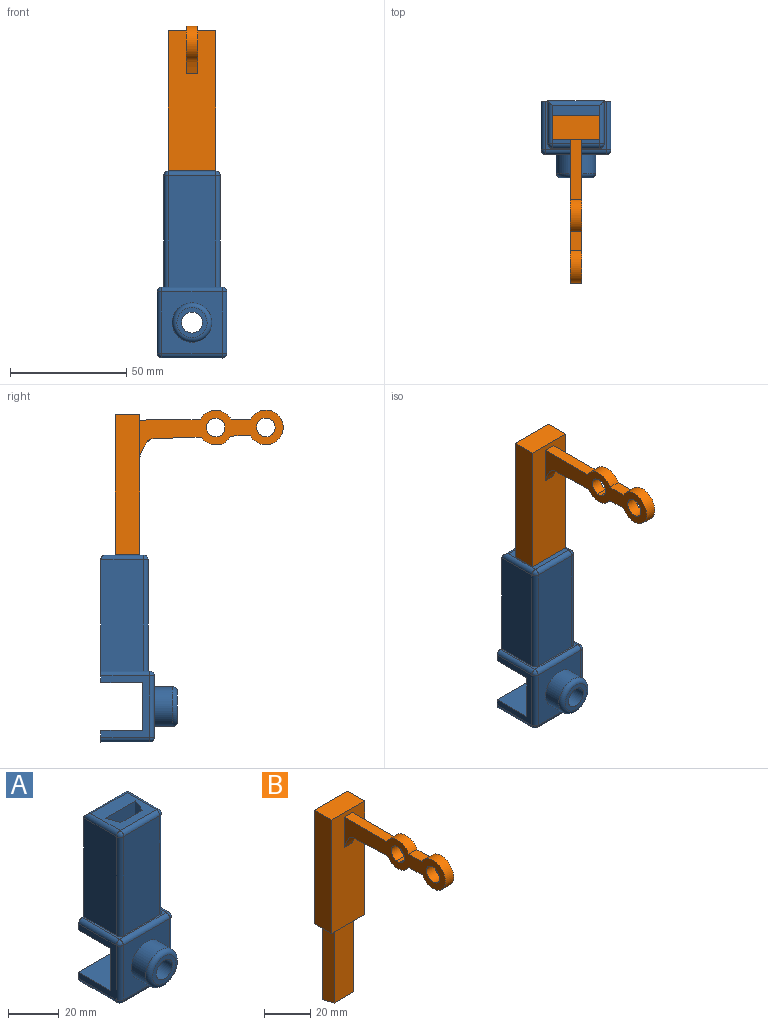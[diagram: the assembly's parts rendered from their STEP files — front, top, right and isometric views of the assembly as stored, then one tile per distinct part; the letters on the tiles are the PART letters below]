
ASSEMBLY  parts=2 mates=1
PART A: 43 faces, bbox 30x33x80.5 mm
  f0: plane 26x21mm, normal (0,0,1), area 54mm2, adj f2,f7,f8,f13,f23,f25,f26,f36
  f1: plane 30x18mm, normal (0,0,-1), area 540mm2, adj f2,f3,f5,f6
  f2: plane 53x30mm, normal (0,1,0), area 1312.8mm2, adj f0,f1,f3,f5,f7,f13,f23,f25
  f3: plane 26.5x21mm, normal (-1,0,0), area 187.5mm2, adj f1,f2,f6,f16,f17,f25,f31,f34
  f4: plane 26.5x26mm, normal (0,-1,0), area 462mm2, adj f20,f26,f27,f31,f32
  f5: plane 26.5x21mm, normal (1,0,0), area 187.5mm2, adj f1,f2,f6,f16,f17,f23,f27,f28
  f6: plane 30x20.5mm, normal (0,1,0), area 551.4mm2, adj f1,f3,f5,f16,f19
  f7: plane 48x18.35mm, normal (-1,0,0), area 880.8mm2, adj f0,f2,f39,f42
  f8: plane 48x20.26mm, normal (0,-1,0), area 972.5mm2, adj f0,f36,f40,f42
  f9: plane 50x16.87mm, normal (0,-1,0), area 843.6mm2, adj f10,f12,f14,f15
  f10: plane 50x6.51mm, normal (-0.94,0.34,0), area 346.4mm2, adj f9,f11,f14,f15
  f11: plane 50x12.13mm, normal (0,1,0), area 606.6mm2, adj f10,f12,f14,f15
  f12: plane 50x6.51mm, normal (0.94,0.34,0), area 346.4mm2, adj f9,f11,f14,f15
  f13: plane 48x18.35mm, normal (1,0,0), area 880.8mm2, adj f0,f2,f35,f36
  f14: plane 20.26x16.35mm, normal (0,0,1), area 236.8mm2, adj f9,f10,f11,f12,f35,f37,f39,f40
  f15: plane 16.87x6.51mm, normal (0,0,1), area 94.4mm2, adj f9,f10,f11,f12
  f16: plane 30x18mm, normal (0,0,1), area 540mm2, adj f3,f5,f6,f17
  f17: plane 30x5mm, normal (0,1,0), area 148.3mm2, adj f3,f5,f16,f18,f28,f34
  f18: plane 26x21mm, normal (0,0,-1), area 546mm2, adj f17,f28,f32,f34
  f19: cylinder r=4.5mm len=15mm, axis (0,1,0), area 424.1mm2, adj f6,f21
  f20: cylinder r=8.5mm len=17mm, axis (0,1,0), area 427.3mm2, adj f4,f22
  f21: plane 13x13mm, normal (0,-1,0), area 69.1mm2, adj f19,f22
  f22: torus R=6.5mm, axis (0,-1,0), area 153.4mm2, adj f20,f21
  f23: cylinder r=2mm len=21mm, axis (0,-1,0), area 66mm2, adj f0,f2,f5,f24
  f24: sphere r=2mm, area 6.3mm2, adj f23,f26,f27
  f25: cylinder r=2mm len=21mm, axis (0,1,0), area 66mm2, adj f0,f2,f3,f29
  f26: cylinder r=2mm len=26mm, axis (-1,0,0), area 81.7mm2, adj f0,f4,f24,f29
  f27: cylinder r=2mm len=26.5mm, axis (0,0,1), area 83.3mm2, adj f4,f5,f24,f30
  f28: cylinder r=2mm len=21mm, axis (0,-1,0), area 66mm2, adj f5,f17,f18,f30
  f29: sphere r=2mm, area 6.3mm2, adj f25,f26,f31
  f30: sphere r=2mm, area 6.3mm2, adj f27,f28,f32
  f31: cylinder r=2mm len=26.5mm, axis (0,0,-1), area 83.3mm2, adj f3,f4,f29,f33
  f32: cylinder r=2mm len=26mm, axis (-1,0,0), area 81.7mm2, adj f4,f18,f30,f33
  f33: sphere r=2mm, area 6.3mm2, adj f31,f32,f34
  f34: cylinder r=2mm len=21mm, axis (0,1,0), area 66mm2, adj f3,f17,f18,f33
  f35: cylinder r=2mm len=18.35mm, axis (0,-1,0), area 55.4mm2, adj f13,f14,f37,f38
  f36: cylinder r=2mm len=48mm, axis (0,0,1), area 150.8mm2, adj f0,f8,f13,f38
  f37: cylinder r=2mm len=24.26mm, axis (1,0,0), area 71.6mm2, adj f2,f14,f35,f39
  f38: sphere r=2mm, area 6.3mm2, adj f35,f36,f40
  f39: cylinder r=2mm len=18.35mm, axis (0,1,0), area 55.4mm2, adj f7,f14,f37,f41
  f40: cylinder r=2mm len=20.26mm, axis (-1,0,0), area 63.6mm2, adj f8,f14,f38,f41
  f41: sphere r=2mm, area 6.3mm2, adj f39,f40,f42
  f42: cylinder r=2mm len=48mm, axis (0,0,-1), area 150.8mm2, adj f0,f7,f8,f41
PART B: 25 faces, bbox 20.3x72.4x102.1 mm
  f0: plane 40x15.87mm, normal (0,1,0), area 634.9mm2, adj f1,f3,f8,f9
  f1: plane 40x5.51mm, normal (-0.94,-0.34,0), area 234.6mm2, adj f0,f2,f3,f8
  f2: plane 40x11.86mm, normal (0,-1,0), area 474.4mm2, adj f1,f3,f8,f9
  f3: plane 15.87x5.51mm, normal (0,0,-1), area 76.4mm2, adj f0,f1,f2,f9
  f4: plane 60x20.26mm, normal (0,-1,0), area 1135.3mm2, adj f6,f7,f8,f10,f11,f12,f13,f14
  f5: plane 60x20.26mm, normal (0,1,0), area 1215.5mm2, adj f6,f7,f8,f10
  f6: plane 60x10.51mm, normal (-1,0,0), area 630.6mm2, adj f4,f5,f7,f8
  f7: plane 20.26x10.51mm, normal (0,0,1), area 212.9mm2, adj f4,f5,f6,f10
  f8: plane 20.26x10.51mm, normal (0,0,-1), area 136.5mm2, adj f0,f1,f2,f4,f5,f6,f9,f10
  f9: plane 40x5.51mm, normal (0.94,-0.34,0), area 234.6mm2, adj f0,f2,f3,f8
  f10: plane 60x10.51mm, normal (1,0,0), area 630.6mm2, adj f4,f5,f7,f8
  f11: extruded ~8.02x5.8mm, area 52mm2, adj f4,f13,f14,f17
  f12: plane 26.04x5mm, normal (0,0,1), area 130.2mm2, adj f4,f13,f14,f18
  f13: plane 61.98x20.48mm, normal (1,0,0), area 517.4mm2, adj f4,f11,f12,f15,f16,f17,f18,f19
  f14: plane 61.98x20.48mm, normal (-1,0,0), area 517.4mm2, adj f4,f11,f12,f15,f16,f17,f18,f19
  f15: cylinder r=7.5mm len=12.82mm, axis (-1,0,0), area 76.9mm2, adj f13,f14,f16,f24
  f16: plane 18.78x5mm, normal (0,-0.03,-1), area 93.9mm2, adj f13,f14,f15,f17
  f17: extruded ~5x1.89mm, area 9.5mm2, adj f11,f13,f14,f16
  f18: cylinder r=7.5mm len=13.41mm, axis (-1,0,0), area 83mm2, adj f12,f13,f14,f19
  f19: plane 8.19x5mm, normal (0,0,1), area 40.9mm2, adj f13,f14,f18,f20
  f20: cylinder r=7.5mm len=15mm, axis (-1,0,0), area 200.2mm2, adj f13,f14,f19,f24
  f21: cylinder r=4mm len=8mm, axis (-1,0,0), area 116.4mm2, adj f13,f14,f22
  f22: plane 5x1.84mm, normal (0,0.03,1), area 9.2mm2, adj f13,f14,f21
  f23: cylinder r=4mm len=8mm, axis (-1,0,0), area 125.7mm2, adj f13,f14
  f24: plane 8.42x5mm, normal (0,-0.03,-1), area 42.1mm2, adj f13,f14,f15,f20
PLACE A rot(axis=(-0.36,0.56,0.75),0deg) t=(13.66,-37.12,-15.78)mm
PLACE B rot(axis=(-0.36,0.56,0.75),0deg) t=(13.66,-37.07,39.64)mm
MATE slider A.f15 <-> B.f3  axis (0,0,1) through (13.66,-36.94,-10.78)mm
